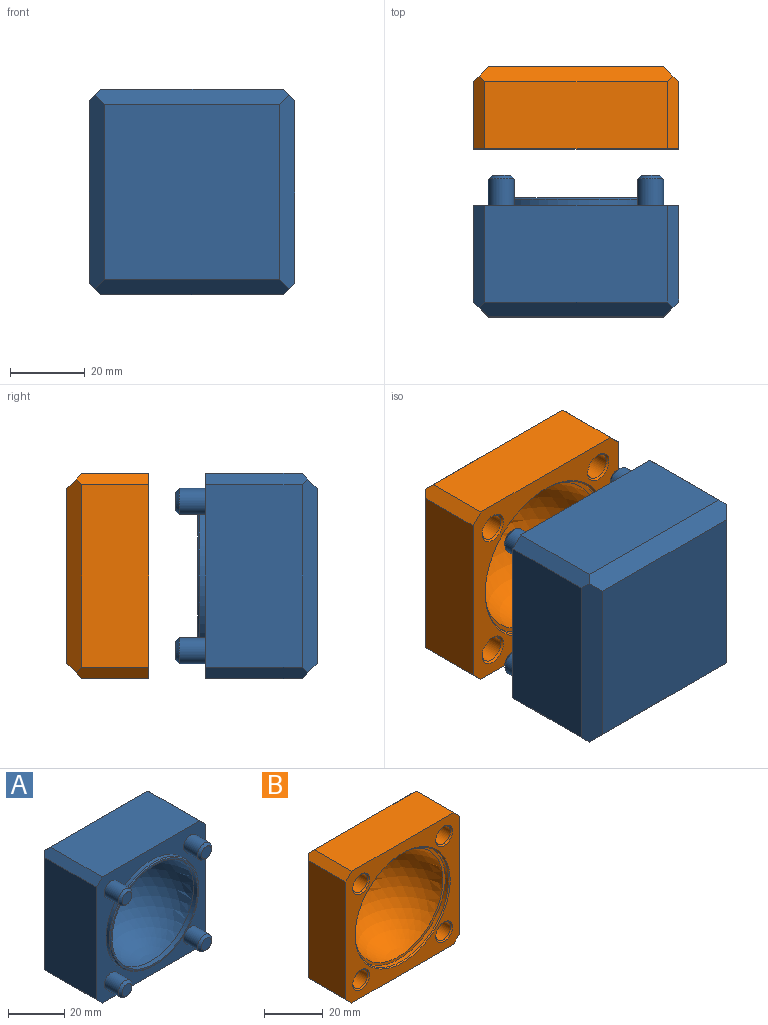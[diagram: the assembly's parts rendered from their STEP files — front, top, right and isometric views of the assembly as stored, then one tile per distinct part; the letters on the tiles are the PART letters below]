
ASSEMBLY  parts=2 mates=1
PART A: 31 faces, bbox 55x38x55 mm
  f0: plane 49x26mm, normal (1,0,0), area 1274mm2, adj f4,f19,f24,f25
  f1: plane 49x26mm, normal (0,0,1), area 1274mm2, adj f4,f21,f22,f25
  f2: plane 49x26mm, normal (-1,0,0), area 1274mm2, adj f4,f20,f22,f23
  f3: plane 49x26mm, normal (0,0,-1), area 1274mm2, adj f4,f18,f23,f24
  f4: plane 55x55mm, normal (0,-1,0), area 1262.6mm2, adj f0,f1,f2,f3,f6,f8,f10,f12
  f5: plane 47x47mm, normal (0,1,0), area 2209mm2, adj f18,f19,f20,f21
  f6: cylinder r=3.5mm len=7mm, axis (0,1,0), area 153.9mm2, adj f4,f17
  f7: plane 5x5mm, normal (0,-1,0), area 19.6mm2, adj f17
  f8: cylinder r=3.5mm len=7mm, axis (0,1,0), area 153.9mm2, adj f4,f14
  f9: plane 5x5mm, normal (0,-1,0), area 19.6mm2, adj f14
  f10: cylinder r=3.5mm len=7mm, axis (0,1,0), area 153.9mm2, adj f4,f15
  f11: plane 5x5mm, normal (0,-1,0), area 19.6mm2, adj f15
  f12: cylinder r=3.5mm len=7mm, axis (0,1,0), area 153.9mm2, adj f4,f16
  f13: plane 5x5mm, normal (0,-1,0), area 19.6mm2, adj f16
  f14: cone r=2.5mm half-angle=45deg, axis (0,1,0), area 26.7mm2, adj f8,f9
  f15: cone r=2.5mm half-angle=45deg, axis (0,1,0), area 26.7mm2, adj f10,f11
  f16: cone r=2.5mm half-angle=45deg, axis (0,1,0), area 26.7mm2, adj f12,f13
  f17: cone r=2.5mm half-angle=45deg, axis (0,1,0), area 26.7mm2, adj f6,f7
  f18: plane 52x4mm, normal (0,0.71,-0.71), area 282.1mm2, adj f3,f5,f19,f20,f23,f24
  f19: plane 52x4mm, normal (0.71,0.71,0), area 282.1mm2, adj f0,f5,f18,f21,f24,f25
  f20: plane 52x4mm, normal (-0.71,0.71,0), area 282.1mm2, adj f2,f5,f18,f21,f22,f23
  f21: plane 52x4mm, normal (0,0.71,0.71), area 282.1mm2, adj f1,f5,f19,f20,f22,f25
  f22: plane 27.5x3mm, normal (-0.71,0,0.71), area 113.5mm2, adj f1,f2,f4,f20,f21
  f23: plane 27.5x3mm, normal (-0.71,0,-0.71), area 113.5mm2, adj f2,f3,f4,f18,f20
  f24: plane 27.5x3mm, normal (0.71,0,-0.71), area 113.5mm2, adj f0,f3,f4,f18,f19
  f25: plane 27.5x3mm, normal (0.71,0,0.71), area 113.5mm2, adj f0,f1,f4,f19,f21
  f26: cylinder r=21.5mm len=43mm, axis (0,1,0), area 270.2mm2, adj f28,f29
  f27: cylinder r=22.5mm len=45mm, axis (0,1,0), area 226.2mm2, adj f4,f30
  f28: plane 44.2x44.2mm, normal (0,-1,0), area 82.2mm2, adj f26,f30
  f29: sphere r=21.5mm, area 2904.4mm2, adj f26
  f30: cone r=22.1mm half-angle=45deg, axis (0,1,0), area 79.3mm2, adj f27,f28
PART B: 31 faces, bbox 55x22x55 mm
  f0: plane 49x18mm, normal (1,0,0), area 882mm2, adj f4,f18,f22,f23
  f1: plane 49x18mm, normal (0,0,1), area 882mm2, adj f4,f19,f22,f25
  f2: plane 49x18mm, normal (-1,0,0), area 882mm2, adj f4,f21,f24,f25
  f3: plane 49x18mm, normal (0,0,-1), area 882mm2, adj f4,f20,f23,f24
  f4: plane 55x55mm, normal (0,-1,0), area 1153.4mm2, adj f0,f1,f2,f3,f14,f15,f16,f17
  f5: plane 47x47mm, normal (0,1,0), area 2130.5mm2, adj f18,f19,f20,f21,f30
  f6: cylinder r=3.55mm len=7.5mm, axis (0,-1,0), area 167.3mm2, adj f7,f17
  f7: plane 7.1x7.1mm, normal (0,-1,0), area 39.6mm2, adj f6
  f8: cylinder r=3.55mm len=7.5mm, axis (0,-1,0), area 167.3mm2, adj f9,f16
  f9: plane 7.1x7.1mm, normal (0,-1,0), area 39.6mm2, adj f8
  f10: cylinder r=3.55mm len=7.5mm, axis (0,-1,0), area 167.3mm2, adj f11,f14
  f11: plane 7.1x7.1mm, normal (0,-1,0), area 39.6mm2, adj f10
  f12: cylinder r=3.55mm len=7.5mm, axis (0,-1,0), area 167.3mm2, adj f13,f15
  f13: plane 7.1x7.1mm, normal (0,-1,0), area 39.6mm2, adj f12
  f14: cone r=3.55mm half-angle=45deg, axis (0,-1,0), area 16.9mm2, adj f4,f10
  f15: cone r=3.55mm half-angle=45deg, axis (0,-1,0), area 16.9mm2, adj f4,f12
  f16: cone r=3.55mm half-angle=45deg, axis (0,-1,0), area 16.9mm2, adj f4,f8
  f17: cone r=3.55mm half-angle=45deg, axis (0,-1,0), area 16.9mm2, adj f4,f6
  f18: plane 52x4mm, normal (0.71,0.71,0), area 282.1mm2, adj f0,f5,f19,f20,f22,f23
  f19: plane 52x4mm, normal (0,0.71,0.71), area 282.1mm2, adj f1,f5,f18,f21,f22,f25
  f20: plane 52x4mm, normal (0,0.71,-0.71), area 282.1mm2, adj f3,f5,f18,f21,f23,f24
  f21: plane 52x4mm, normal (-0.71,0.71,0), area 282.1mm2, adj f2,f5,f19,f20,f24,f25
  f22: plane 19.5x3mm, normal (0.71,0,0.71), area 79.5mm2, adj f0,f1,f4,f18,f19
  f23: plane 19.5x3mm, normal (0.71,0,-0.71), area 79.5mm2, adj f0,f3,f4,f18,f20
  f24: plane 19.5x3mm, normal (-0.71,0,-0.71), area 79.5mm2, adj f2,f3,f4,f20,f21
  f25: plane 19.5x3mm, normal (-0.71,0,0.71), area 79.5mm2, adj f1,f2,f4,f19,f21
  f26: cylinder r=22.5mm len=45mm, axis (0,-1,0), area 226.2mm2, adj f27,f29
  f27: plane 45x45mm, normal (0,-1,0), area 150.8mm2, adj f26,f28
  f28: sphere r=21.5mm, area 2549.5mm2, adj f27,f30
  f29: cone r=22.5mm half-angle=45deg, axis (0,-1,0), area 80.7mm2, adj f4,f26
  f30: cylinder r=5mm len=10mm, axis (0,1,0), area 34.2mm2, adj f5,f28
PLACE A rot(axis=(-0.71,0,-0.71),180deg) t=(11.4,-65.96,-3.48)mm
PLACE B t=(11.4,1.14,-3.48)mm
MATE slider B.f6 <-> A.f8  axis (0,-1,0) through (-8.6,-12.86,16.52)mm
